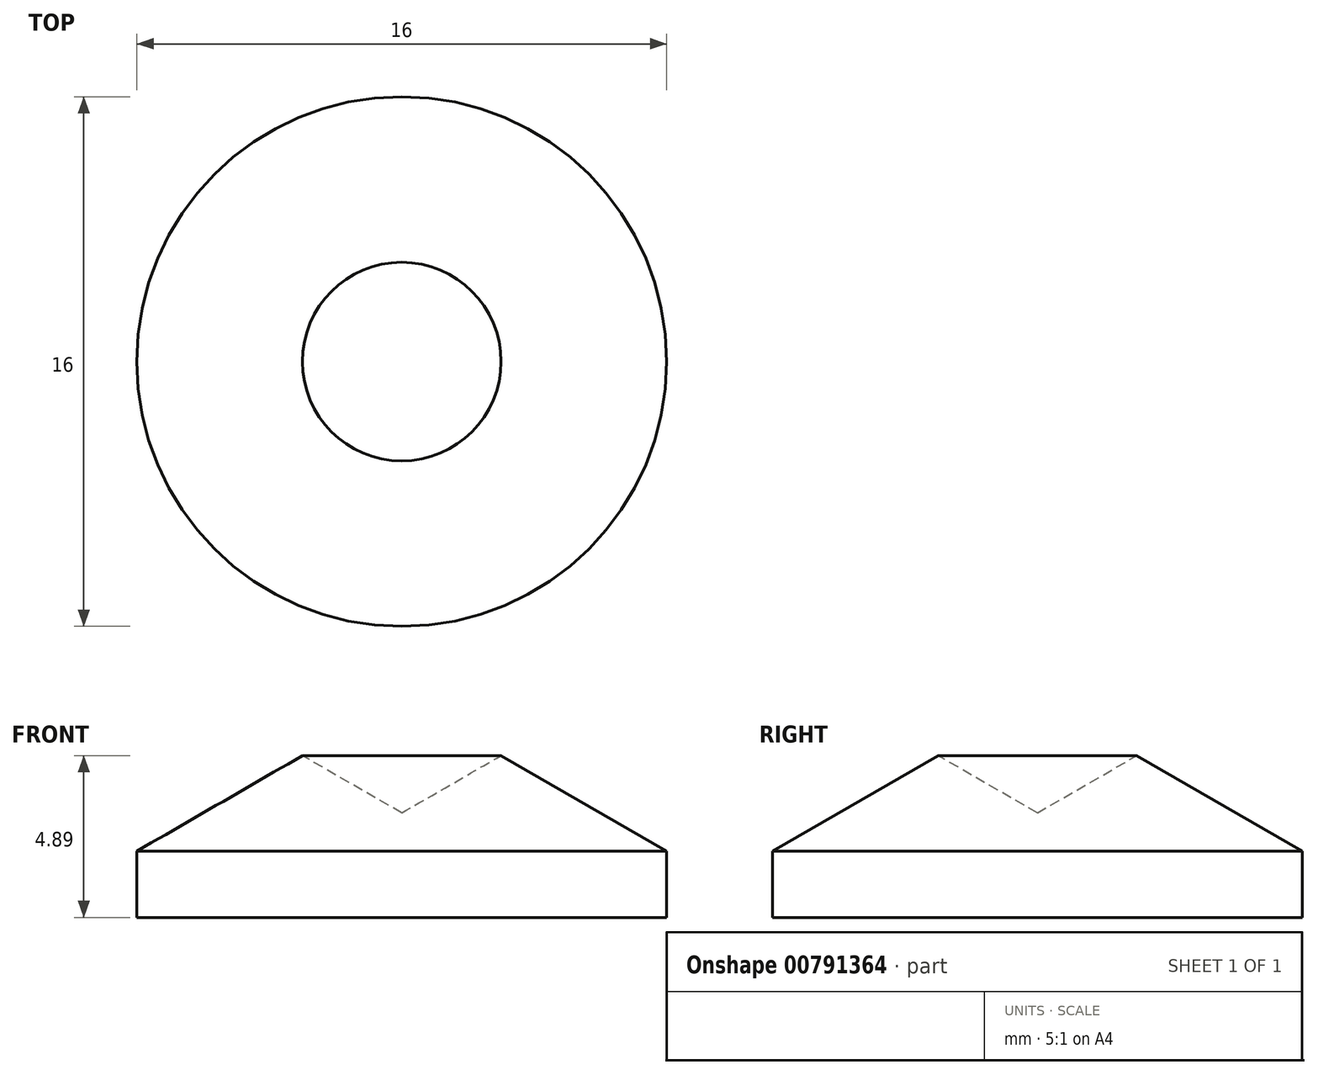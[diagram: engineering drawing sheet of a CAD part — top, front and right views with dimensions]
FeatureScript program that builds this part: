
annotation { "Feature Type Name" : "Feature", "Feature Type Description" : "" }
export const myFeature = defineFeature(function(context is Context, id is Id, definition is map)
    precondition{}
    {
        {
            var Q0;
            Q0=qCreatedBy(makeId("Front.planeOp"),FACE);
            var sketch = newSketch(context, id + "F0", { "sketchPlane" : qUnion([Q0])});
            skLineSegment(sketch, "E0", {"start": v(-8, 0) * mm, "end": v(0, 0) * mm});
            skLineSegment(sketch, "E1", {"start": v(0, 0) * mm, "end": v(0, 3.15) * mm});
            skLineSegment(sketch, "E2", {"start": v(0, 3.15) * mm, "end": v(-3, 4.89) * mm});
            skLineSegment(sketch, "E3", {"start": v(-3, 4.89) * mm, "end": v(-8, 2) * mm});
            skLineSegment(sketch, "E4", {"start": v(-8, 2) * mm, "end": v(-8, 0) * mm});
            skSolve(sketch);
        }
        {
            var Q0;
            Q0 = qSketchRegion(id + "F0", true);
            var Q1;
            Q1=sQuery(id+"F0.wireOp",EDGE,"E1");
            revolve(context, id + "F1", {"surfaceOperationType" : NewSurfaceOperationType.NEW, "entities" : qUnion([Q0]), "axis" : qUnion([Q1]), "revolveType" : RevolveType.FULL});
        }
    });
